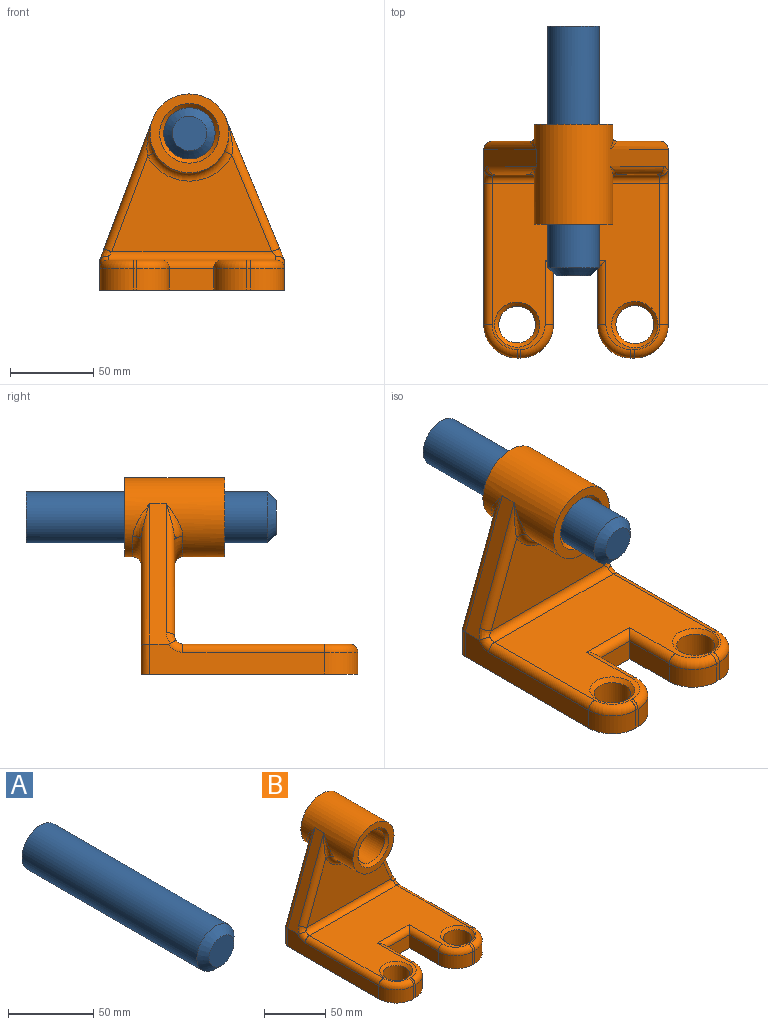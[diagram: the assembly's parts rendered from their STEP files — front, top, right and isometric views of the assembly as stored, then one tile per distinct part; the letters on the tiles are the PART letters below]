
ASSEMBLY  parts=2 mates=1
PART A: 4 faces, bbox 30.8x150x30.8 mm
  f0: cylinder r=15.38mm len=145mm, axis (0,1,0), area 14012.1mm2, adj f2,f3
  f1: plane 20.76x20.76mm, normal (0,-1,0), area 338.5mm2, adj f3
  f2: plane 30.76x30.76mm, normal (0,1,0), area 743.1mm2, adj f0
  f3: cone r=10.38mm half-angle=45deg, axis (0,1,0), area 572.2mm2, adj f0,f1
PART B: 68 faces, bbox 114x141.6x117.7 mm
  f0: plane 13.02x1.78mm, normal (0,-1,0), area 23.1mm2, adj f1,f8,f14,f51
  f1: plane 130x110.68mm, normal (0,0,-1), area 3961.4mm2, adj f0,f3,f4,f5,f6,f7,f8,f9
  f2: plane 100.68x100mm, normal (0,0,1), area 6739.5mm2, adj f36,f37,f38,f39,f42,f43,f46,f47
  f3: plane 105x18.02mm, normal (-1,0,0), area 1436.4mm2, adj f1,f8,f17,f55,f56,f59
  f4: plane 105x18.02mm, normal (1,0,0), area 1436.4mm2, adj f1,f7,f16,f46,f50,f57
  f5: plane 100.68x81.04mm, normal (0,1,0), area 5978.9mm2, adj f1,f57,f58,f59,f61,f62
  f6: plane 13.02x2.4mm, normal (0,-1,0), area 31.2mm2, adj f1,f7,f15,f38
  f7: cylinder r=20mm len=20mm, axis (0,0,-1), area 409mm2, adj f1,f4,f6,f42
  f8: cylinder r=20mm len=20mm, axis (0,0,1), area 409mm2, adj f0,f1,f3,f54
  f9: cylinder r=11.01mm len=22.03mm, axis (0,0,1), area 1074mm2, adj f1,f67
  f10: cylinder r=11.43mm len=22.85mm, axis (0,0,1), area 1114.3mm2, adj f1,f66
  f11: plane 33.48x13.02mm, normal (-1,0,0), area 435.9mm2, adj f1,f13,f15,f37
  f12: plane 33.48x13.02mm, normal (1,0,0), area 435.9mm2, adj f1,f13,f14,f43
  f13: plane 26.51x13.02mm, normal (0,-1,0), area 345.1mm2, adj f1,f11,f12,f39
  f14: cylinder r=20mm len=20mm, axis (0,0,-1), area 409mm2, adj f0,f1,f12,f47
  f15: cylinder r=20mm len=20mm, axis (0,0,1), area 409mm2, adj f1,f6,f11,f36
  f16: plane 85.04x34.99mm, normal (0.92,0,0.38), area 925.9mm2, adj f4,f20,f45,f49,f50,f58
  f17: plane 84.35x31.65mm, normal (-0.94,0,0.35), area 906.7mm2, adj f3,f20,f48,f52,f55,f61
  f18: plane 96x58.02mm, normal (0,-1,0), area 3675.1mm2, adj f40,f45,f48,f53
  f19: cylinder r=15.38mm len=55mm, axis (0,1,0), area 5314.7mm2, adj f64,f65
  f20: cylinder r=23.66mm len=60mm, axis (0,1,0), area 6532.8mm2, adj f16,f17,f21,f22,f40,f41,f44,f60
  f21: plane 47.33x47.33mm, normal (0,-1,0), area 755.1mm2, adj f20,f65
  f22: plane 47.33x47.33mm, normal (0,1,0), area 755.1mm2, adj f20,f64
  f23: cylinder r=21.38mm len=41.69mm, axis (0,1,0), area 460.8mm2, adj f27,f33,f34,f35
  f24: plane 98.68x90.1mm, normal (0,0,-1), area 7074.7mm2, adj f25,f26,f28,f29,f30,f31,f32,f35
  f25: plane 94.33x16.93mm, normal (1,0,0), area 1173.2mm2, adj f1,f24,f27,f28,f34,f35
  f26: plane 93.62x16.83mm, normal (-1,0,0), area 1163.8mm2, adj f1,f24,f27,f29,f33,f35
  f27: plane 98.68x89.64mm, normal (0,-1,0), area 6233mm2, adj f1,f23,f25,f26,f33,f34
  f28: cylinder r=17.01mm len=29.78mm, axis (0,0,1), area 440.4mm2, adj f1,f24,f25,f31
  f29: cylinder r=17.43mm len=30.4mm, axis (0,0,1), area 452.1mm2, adj f1,f24,f26,f30
  f30: plane 33.58x12.02mm, normal (1,0,0), area 403.6mm2, adj f1,f24,f29,f32
  f31: plane 33.11x12.02mm, normal (-1,0,0), area 398mm2, adj f1,f24,f28,f32
  f32: plane 38.51x12.02mm, normal (0,1,0), area 462.8mm2, adj f1,f24,f30,f31
  f33: plane 72.81x29.96mm, normal (-0.92,0,-0.38), area 629.8mm2, adj f23,f26,f27,f35
  f34: plane 72.05x27.03mm, normal (0.94,0,-0.35), area 615.7mm2, adj f23,f25,f27,f35
  f35: plane 98.68x77.62mm, normal (0,1,0), area 5046.9mm2, adj f23,f24,f25,f26,f33,f34
  f36: torus R=15mm, axis (0,0,1), area 224.3mm2, adj f2,f15,f37,f38
  f37: cylinder r=5mm len=38.48mm, axis (0,-1,0), area 282.6mm2, adj f2,f11,f36,f39
  f38: cylinder r=5mm len=5mm, axis (1,0,0), area 18.8mm2, adj f2,f6,f36,f42
  f39: cylinder r=5mm len=36.51mm, axis (1,0,0), area 247.4mm2, adj f2,f13,f37,f43
  f40: torus R=28.66mm, axis (0,-1,0), area 433.8mm2, adj f18,f20,f41,f44
  f41: bspline ~24.05x10mm, area 56.4mm2, adj f20,f40,f45
  f42: torus R=15mm, axis (0,0,1), area 224.3mm2, adj f2,f7,f38,f46
  f43: cylinder r=5mm len=38.48mm, axis (0,1,0), area 282.6mm2, adj f2,f12,f39,f47
  f44: bspline ~24.15x10mm, area 55.9mm2, adj f20,f40,f48
  f45: cylinder r=5mm len=80.04mm, axis (0.38,0,-0.92), area 578.2mm2, adj f16,f18,f41,f49
  f46: cylinder r=5mm len=85mm, axis (0,1,0), area 667.6mm2, adj f2,f4,f42,f50
  f47: torus R=15mm, axis (0,0,1), area 224.3mm2, adj f2,f14,f43,f51
  f48: cylinder r=5mm len=79.35mm, axis (0.35,0,0.94), area 565.5mm2, adj f17,f18,f44,f52
  f49: bspline ~7.84x7.82mm, area 39.9mm2, adj f16,f45,f50,f53
  f50: torus R=10mm, axis (1,0,0), area 53.8mm2, adj f4,f16,f46,f49,f53
  f51: cylinder r=5mm len=5mm, axis (1,0,0), area 14mm2, adj f0,f2,f47,f54
  f52: bspline ~7.12x6.49mm, area 38.6mm2, adj f17,f48,f53,f55
  f53: cylinder r=5mm len=100.68mm, axis (-1,0,0), area 783.3mm2, adj f2,f18,f49,f50,f52,f55
  f54: torus R=15mm, axis (0,0,1), area 224.3mm2, adj f2,f8,f51,f56
  f55: torus R=10mm, axis (1,0,0), area 54mm2, adj f3,f17,f52,f53,f56
  f56: cylinder r=5mm len=85mm, axis (0,-1,0), area 667.6mm2, adj f2,f3,f54,f55
  f57: cylinder r=5mm len=18.02mm, axis (0,0,1), area 137.6mm2, adj f1,f4,f5,f58
  f58: cylinder r=5mm len=86.94mm, axis (-0.38,0,0.92), area 632.9mm2, adj f5,f16,f57,f60
  f59: cylinder r=5mm len=18.02mm, axis (0,0,-1), area 138mm2, adj f1,f3,f5,f61
  f60: bspline ~22.56x10mm, area 78.9mm2, adj f20,f58,f62
  f61: cylinder r=5mm len=86.11mm, axis (-0.35,0,-0.94), area 618.6mm2, adj f5,f17,f59,f63
  f62: torus R=28.66mm, axis (0,-1,0), area 433.8mm2, adj f5,f20,f60,f63
  f63: bspline ~24.15x10mm, area 56.4mm2, adj f20,f61,f62
  f64: cone r=17.88mm half-angle=45deg, axis (0,1,0), area 369.4mm2, adj f19,f22
  f65: cone r=15.38mm half-angle=45deg, axis (0,-1,0), area 369.4mm2, adj f19,f21
  f66: cone r=11.43mm half-angle=45deg, axis (0,0,1), area 281.6mm2, adj f2,f10
  f67: cone r=11.01mm half-angle=45deg, axis (0,0,1), area 272.4mm2, adj f2,f9
PLACE A rot(axis=(0,-1,0),136.6deg) t=(-28.44,150.93,38.25)mm
PLACE B t=(-28.44,156.86,0.63)mm fixed
MATE cylindrical B.f19 <-> A.f0  axis (0,1,0) through (-28.44,109.36,38.25)mm
